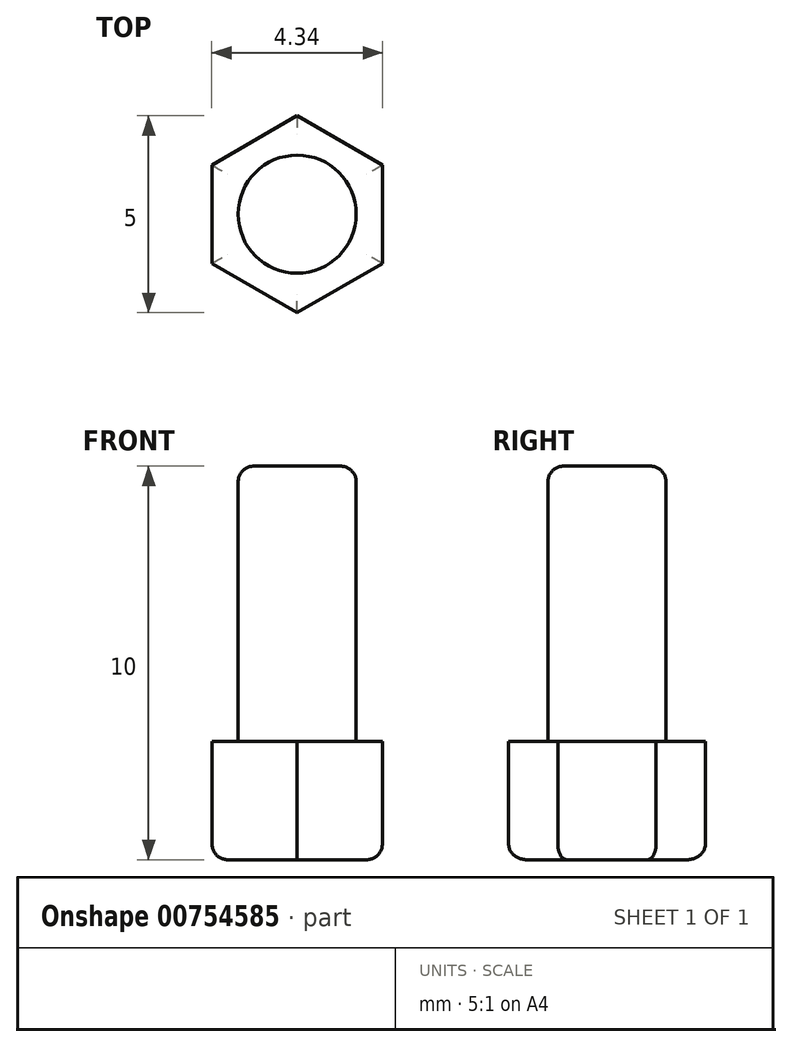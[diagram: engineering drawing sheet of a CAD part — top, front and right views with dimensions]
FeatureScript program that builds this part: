
annotation { "Feature Type Name" : "Feature", "Feature Type Description" : "" }
export const myFeature = defineFeature(function(context is Context, id is Id, definition is map)
    precondition{}
    {
        {
            var Q0;
            Q0=qCreatedBy(makeId("Top.planeOp"),FACE);
            var sketch = newSketch(context, id + "F0", { "sketchPlane" : qUnion([Q0])});
            skCircle(sketch, "E0.cCircle", {"center": v(0, 0) * mm, "radius": 2.5 * mm, "construction": true});
            skLineSegment(sketch, "E0.0", {"start": v(0, 2.5) * mm, "end": v(2.17, 1.25) * mm});
            skLineSegment(sketch, "E0.1", {"start": v(2.17, 1.25) * mm, "end": v(2.17, -1.25) * mm});
            skLineSegment(sketch, "E0.2", {"start": v(2.17, -1.25) * mm, "end": v(0, -2.5) * mm});
            skLineSegment(sketch, "E0.3", {"start": v(0, -2.5) * mm, "end": v(-2.17, -1.25) * mm});
            skLineSegment(sketch, "E0.4", {"start": v(-2.17, -1.25) * mm, "end": v(-2.17, 1.25) * mm});
            skLineSegment(sketch, "E0.5", {"start": v(-2.17, 1.25) * mm, "end": v(0, 2.5) * mm});
            skSolve(sketch);
        }
        {
            var Q0;
            Q0 = qSketchRegion(id + "F0", true);
            extrude(context, id + "F1", {"entities" : qUnion([Q0]), "depth" : 3 * mm, "offsetDistance" : 25 * mm});
        }
        {
            var Q0;
            Q0=makeQuery(id+"F1.opExtrude","CAP_FACE",FACE,{"disambiguationData":[OSD([sQuery(id+"F0.wireOp",EDGE,"E0.0"),sQuery(id+"F0.wireOp",EDGE,"E0.1"),sQuery(id+"F0.wireOp",EDGE,"E0.2"),sQuery(id+"F0.wireOp",EDGE,"E0.3"),sQuery(id+"F0.wireOp",EDGE,"E0.4"),sQuery(id+"F0.wireOp",EDGE,"E0.5")])],"isStart":false});
            var sketch = newSketch(context, id + "F2", { "sketchPlane" : qUnion([Q0])});
            skCircle(sketch, "E1", {"center": v(0, 0) * mm, "radius": 1.5 * mm});
            skSolve(sketch);
        }
        {
            var Q0;
            Q0 = qSketchRegion(id + "F2", true);
            extrude(context, id + "F3", {"entities" : qUnion([Q0]), "operationType" : NewBodyOperationType.ADD, "depth" : 7 * mm, "offsetDistance" : 25 * mm});
        }
        {
            var Q0;
            Q0=makeQuery(id+"F1.opExtrude","CAP_EDGE",EDGE,{"disambiguationData":[OSD([sQuery(id+"F0.wireOp",EDGE,"E0.5")])],"isStart":true});
            var Q1;
            Q1=makeQuery(id+"F1.opExtrude","CAP_EDGE",EDGE,{"disambiguationData":[OSD([sQuery(id+"F0.wireOp",EDGE,"E0.4")])],"isStart":true});
            var Q2;
            Q2=makeQuery(id+"F1.opExtrude","CAP_EDGE",EDGE,{"disambiguationData":[OSD([sQuery(id+"F0.wireOp",EDGE,"E0.3")])],"isStart":true});
            var Q3;
            Q3=makeQuery(id+"F1.opExtrude","CAP_EDGE",EDGE,{"disambiguationData":[OSD([sQuery(id+"F0.wireOp",EDGE,"E0.2")])],"isStart":true});
            var Q4;
            Q4=makeQuery(id+"F1.opExtrude","CAP_EDGE",EDGE,{"disambiguationData":[OSD([sQuery(id+"F0.wireOp",EDGE,"E0.1")])],"isStart":true});
            var Q5;
            Q5=makeQuery(id+"F1.opExtrude","CAP_EDGE",EDGE,{"disambiguationData":[OSD([sQuery(id+"F0.wireOp",EDGE,"E0.0")])],"isStart":true});
            var Q6;
            Q6=makeQuery(id+"F3.opExtrude","CAP_EDGE",EDGE,{"disambiguationData":[OSD([sQuery(id+"F2.wireOp",EDGE,"E1")])],"isStart":false});
            fillet(context, id + "F4", {"entities" : qUnion([Q0, Q1, Q2, Q3, Q4, Q5, Q6]), "radius" : .4 * mm, "tangentPropagation" : true, "allowEdgeOverflow" : false});
        }
    });
